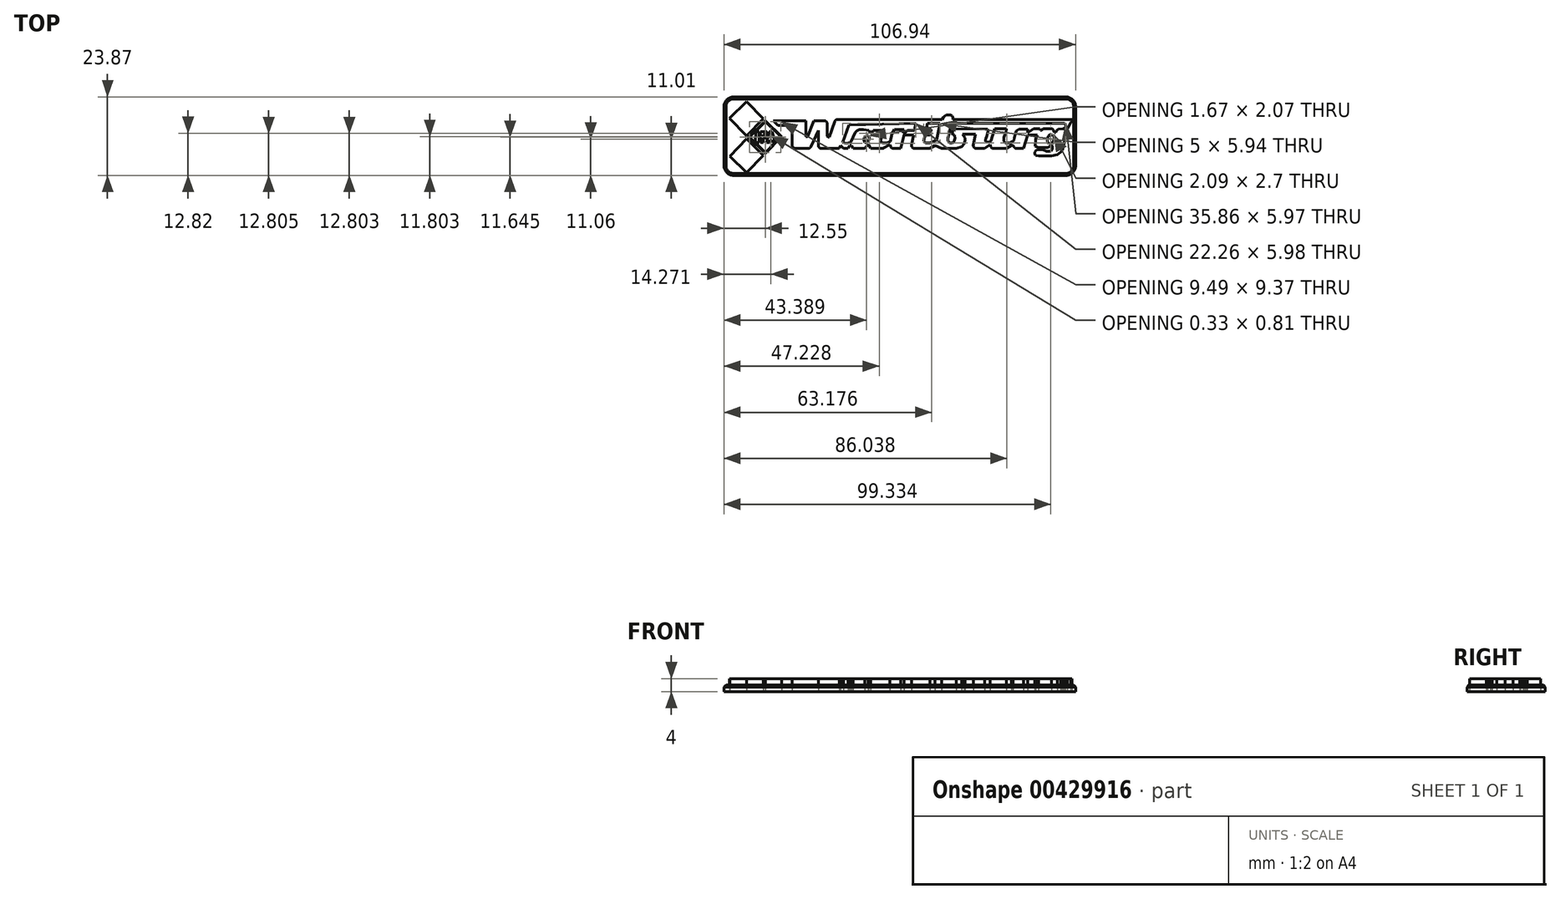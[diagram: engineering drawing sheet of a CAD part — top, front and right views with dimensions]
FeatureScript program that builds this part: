
annotation { "Feature Type Name" : "Feature", "Feature Type Description" : "" }
export const myFeature = defineFeature(function(context is Context, id is Id, definition is map)
    precondition{}
    {
        {
            var Q0;
            Q0=qCreatedBy(makeId("Top.planeOp"),FACE);
            var sketch = newSketch(context, id + "F0", { "sketchPlane" : qUnion([Q0])});
            skLineSegment(sketch, "E0", {"start": v(-43.55, 10.1) * mm, "end": v(-42.14, 8.69) * mm});
            skLineSegment(sketch, "E1", {"start": v(-42.14, 8.69) * mm, "end": v(-37.83, 8.69) * mm});
            skLineSegment(sketch, "E2", {"start": v(-37.83, 8.69) * mm, "end": v(-37.83, 2.66) * mm});
            skLineSegment(sketch, "E3", {"start": v(-36.83, 1.66) * mm, "end": v(-33.06, 1.66) * mm});
            skLineSegment(sketch, "E4", {"start": v(-32.15, 2.25) * mm, "end": v(-29.9, 7.18) * mm});
            skLineSegment(sketch, "E5", {"start": v(-29.9, 7.18) * mm, "end": v(-29.9, 2.66) * mm});
            skLineSegment(sketch, "E6", {"start": v(-28.9, 1.66) * mm, "end": v(-23.48, 1.66) * mm});
            skLineSegment(sketch, "E7", {"start": v(-23.48, 1.66) * mm, "end": v(-23.07, 2.58) * mm});
            skLineSegment(sketch, "E8", {"start": v(-23.07, 2.58) * mm, "end": v(-22.26, 1.66) * mm});
            skLineSegment(sketch, "E9", {"start": v(-22.26, 1.66) * mm, "end": v(-20.78, 1.66) * mm});
            skLineSegment(sketch, "E10", {"start": v(-20.78, 1.66) * mm, "end": v(-20.37, 2.58) * mm});
            skLineSegment(sketch, "E11", {"start": v(-20.37, 2.58) * mm, "end": v(-19.82, 2.58) * mm});
            skLineSegment(sketch, "E12", {"start": v(-19.82, 2.58) * mm, "end": v(-19.33, 1.66) * mm});
            skLineSegment(sketch, "E13", {"start": v(-19.33, 1.66) * mm, "end": v(-15.78, 1.66) * mm});
            skLineSegment(sketch, "E14", {"start": v(-15.78, 1.66) * mm, "end": v(-14.79, 2.94) * mm});
            skLineSegment(sketch, "E15", {"start": v(-14.79, 2.94) * mm, "end": v(-14.56, 2.83) * mm});
            skLineSegment(sketch, "E16", {"start": v(-14.56, 2.83) * mm, "end": v(-14.04, 1.66) * mm});
            skLineSegment(sketch, "E17", {"start": v(-14.04, 1.66) * mm, "end": v(-10.49, 1.66) * mm});
            skLineSegment(sketch, "E18", {"start": v(-10, 1.8) * mm, "end": v(-8.19, 2.83) * mm});
            skLineSegment(sketch, "E19", {"start": v(-8.19, 2.83) * mm, "end": v(-7.93, 2.26) * mm});
            skLineSegment(sketch, "E20", {"start": v(-7.02, 1.66) * mm, "end": v(-4.8, 1.66) * mm});
            skLineSegment(sketch, "E21", {"start": v(-4.8, 1.66) * mm, "end": v(-3.85, 5.72) * mm});
            skLineSegment(sketch, "E22", {"start": v(-3.85, 5.72) * mm, "end": v(-0.92, 5.72) * mm});
            skLineSegment(sketch, "E23", {"start": v(-0.92, 5.72) * mm, "end": v(-1.55, 2.88) * mm});
            skLineSegment(sketch, "E24", {"start": v(-0.57, 1.66) * mm, "end": v(4.03, 1.66) * mm});
            skLineSegment(sketch, "E25", {"start": v(4.03, 1.66) * mm, "end": v(5.61, 2.58) * mm});
            skLineSegment(sketch, "E26", {"start": v(5.61, 2.58) * mm, "end": v(7.62, 1.66) * mm});
            skLineSegment(sketch, "E27", {"start": v(7.62, 1.66) * mm, "end": v(12.02, 1.66) * mm});
            skLineSegment(sketch, "E28", {"start": v(12.02, 1.66) * mm, "end": v(13.67, 2.22) * mm});
            skLineSegment(sketch, "E29", {"start": v(13.67, 2.22) * mm, "end": v(14.43, 3.1) * mm});
            skLineSegment(sketch, "E30", {"start": v(14.43, 3.1) * mm, "end": v(14.66, 4.08) * mm});
            skLineSegment(sketch, "E31", {"start": v(14.66, 4.08) * mm, "end": v(14.66, 4.86) * mm});
            skLineSegment(sketch, "E32", {"start": v(14.66, 4.86) * mm, "end": v(14.32, 5.45) * mm});
            skLineSegment(sketch, "E33", {"start": v(14.32, 5.45) * mm, "end": v(13.97, 6.06) * mm});
            skLineSegment(sketch, "E34", {"start": v(13.97, 6.06) * mm, "end": v(17.89, 6.06) * mm});
            skLineSegment(sketch, "E35", {"start": v(17.89, 6.06) * mm, "end": v(17.22, 2.87) * mm});
            skLineSegment(sketch, "E36", {"start": v(18.2, 1.66) * mm, "end": v(20.67, 1.66) * mm});
            skLineSegment(sketch, "E37", {"start": v(20.67, 1.66) * mm, "end": v(22.38, 2.83) * mm});
            skLineSegment(sketch, "E38", {"start": v(22.38, 2.83) * mm, "end": v(22.43, 2.52) * mm});
            skLineSegment(sketch, "E39", {"start": v(23.42, 1.66) * mm, "end": v(27.3, 1.66) * mm});
            skLineSegment(sketch, "E40", {"start": v(27.3, 1.66) * mm, "end": v(28.86, 2.56) * mm});
            skLineSegment(sketch, "E41", {"start": v(28.86, 2.56) * mm, "end": v(29.36, 2.56) * mm});
            skLineSegment(sketch, "E42", {"start": v(29.36, 2.56) * mm, "end": v(29.59, 2.17) * mm});
            skLineSegment(sketch, "E43", {"start": v(30.45, 1.66) * mm, "end": v(32.55, 1.66) * mm});
            skLineSegment(sketch, "E44", {"start": v(32.55, 1.66) * mm, "end": v(33.8, 5.8) * mm});
            skLineSegment(sketch, "E45", {"start": v(33.8, 5.8) * mm, "end": v(36.68, 5.8) * mm});
            skLineSegment(sketch, "E46", {"start": v(36.68, 5.8) * mm, "end": v(36.24, 4.52) * mm});
            skLineSegment(sketch, "E47", {"start": v(36.24, 4.52) * mm, "end": v(36.05, 2.39) * mm});
            skLineSegment(sketch, "E48", {"start": v(36.05, 2.39) * mm, "end": v(37.02, 1.95) * mm});
            skLineSegment(sketch, "E49", {"start": v(37.02, 1.95) * mm, "end": v(40.01, 1.95) * mm});
            skLineSegment(sketch, "E50", {"start": v(40.01, 1.95) * mm, "end": v(40.77, 2.56) * mm});
            skLineSegment(sketch, "E51", {"start": v(40.77, 2.56) * mm, "end": v(41.17, 2.56) * mm});
            skLineSegment(sketch, "E52", {"start": v(41.17, 2.56) * mm, "end": v(41.33, 2.49) * mm});
            skLineSegment(sketch, "E53", {"start": v(41.33, 2.49) * mm, "end": v(41.33, 1.66) * mm});
            skLineSegment(sketch, "E54", {"start": v(41.33, 1.66) * mm, "end": v(40.92, 0.77) * mm});
            skLineSegment(sketch, "E55", {"start": v(40.92, 0.77) * mm, "end": v(39.5, 0.77) * mm});
            skLineSegment(sketch, "E56", {"start": v(39.5, 0.77) * mm, "end": v(38.83, 1.08) * mm});
            skLineSegment(sketch, "E57", {"start": v(38.83, 1.08) * mm, "end": v(38.33, 1.31) * mm});
            skLineSegment(sketch, "E58", {"start": v(38.33, 1.31) * mm, "end": v(36.74, 1.31) * mm});
            skLineSegment(sketch, "E59", {"start": v(36.74, 1.31) * mm, "end": v(36.28, 1.04) * mm});
            skLineSegment(sketch, "E60", {"start": v(36.28, 1.04) * mm, "end": v(35.88, 0.62) * mm});
            skLineSegment(sketch, "E61", {"start": v(35.88, 0.62) * mm, "end": v(35.88, 0) * mm});
            skLineSegment(sketch, "E62", {"start": v(35.88, 0) * mm, "end": v(36.14, -0.46) * mm});
            skLineSegment(sketch, "E63", {"start": v(36.14, -0.46) * mm, "end": v(37.02, -0.63) * mm});
            skLineSegment(sketch, "E64", {"start": v(37.02, -0.63) * mm, "end": v(39.02, -0.63) * mm});
            skLineSegment(sketch, "E65", {"start": v(39.02, -0.63) * mm, "end": v(41, -0.63) * mm});
            skLineSegment(sketch, "E66", {"start": v(41, -0.63) * mm, "end": v(42.73, -0.23) * mm});
            skLineSegment(sketch, "E67", {"start": v(42.73, -0.23) * mm, "end": v(43.85, 0.62) * mm});
            skLineSegment(sketch, "E68", {"start": v(43.85, 0.62) * mm, "end": v(44.3, 1.19) * mm});
            skLineSegment(sketch, "E69", {"start": v(44.3, 1.19) * mm, "end": v(44.65, 2.56) * mm});
            skLineSegment(sketch, "E70", {"start": v(44.65, 2.56) * mm, "end": v(45.18, 5.05) * mm});
            skLineSegment(sketch, "E71", {"start": v(45.18, 5.05) * mm, "end": v(45.85, 7.5) * mm});
            skLineSegment(sketch, "E72", {"start": v(45.85, 7.5) * mm, "end": v(46.42, 8.72) * mm});
            skLineSegment(sketch, "E73", {"start": v(46.42, 8.72) * mm, "end": v(46.81, 9.59) * mm});
            skLineSegment(sketch, "E74", {"start": v(46.81, 9.59) * mm, "end": v(47.17, 9.8) * mm});
            skLineSegment(sketch, "E75", {"start": v(47.17, 9.8) * mm, "end": v(47.17, 10.53) * mm});
            skLineSegment(sketch, "E76", {"start": v(47.17, 10.53) * mm, "end": v(11.1, 10.53) * mm});
            skLineSegment(sketch, "E77", {"start": v(11.1, 10.53) * mm, "end": v(11.1, 11.1) * mm});
            skLineSegment(sketch, "E78", {"start": v(11.1, 11.1) * mm, "end": v(10.83, 11.57) * mm});
            skLineSegment(sketch, "E79", {"start": v(10.83, 11.57) * mm, "end": v(10.27, 11.83) * mm});
            skLineSegment(sketch, "E80", {"start": v(10.27, 11.83) * mm, "end": v(9.03, 11.83) * mm});
            skLineSegment(sketch, "E81", {"start": v(9.03, 11.83) * mm, "end": v(8.48, 11.51) * mm});
            skLineSegment(sketch, "E82", {"start": v(8.48, 11.51) * mm, "end": v(8.06, 11.08) * mm});
            skLineSegment(sketch, "E83", {"start": v(8.06, 11.08) * mm, "end": v(7.67, 10.53) * mm});
            skLineSegment(sketch, "E84", {"start": v(7.67, 10.53) * mm, "end": v(-24, 10.53) * mm});
            skLineSegment(sketch, "E85", {"start": v(-24.94, 9.85) * mm, "end": v(-26.57, 5.09) * mm});
            skLineSegment(sketch, "E86", {"start": v(-26.57, 5.09) * mm, "end": v(-26.99, 5.09) * mm});
            skLineSegment(sketch, "E87", {"start": v(-26.99, 5.09) * mm, "end": v(-27.15, 5.37) * mm});
            skLineSegment(sketch, "E88", {"start": v(-27.15, 5.37) * mm, "end": v(-27.15, 9.1) * mm});
            skLineSegment(sketch, "E89", {"start": v(-28.15, 10.1) * mm, "end": v(-31.3, 10.1) * mm});
            skLineSegment(sketch, "E90", {"start": v(-31.3, 10.1) * mm, "end": v(-33.2, 5.32) * mm});
            skLineSegment(sketch, "E91", {"start": v(-33.2, 5.32) * mm, "end": v(-33.63, 5.32) * mm});
            skLineSegment(sketch, "E92", {"start": v(-33.63, 5.32) * mm, "end": v(-33.63, 10.1) * mm});
            skLineSegment(sketch, "E93", {"start": v(-33.63, 10.1) * mm, "end": v(-43.55, 10.1) * mm});
            skLineSegment(sketch, "E94", {"start": v(-45.97, 10.1) * mm, "end": v(-41.01, 5.28) * mm});
            skLineSegment(sketch, "E95", {"start": v(-41.01, 5.28) * mm, "end": v(-45.99, 0.15) * mm});
            skLineSegment(sketch, "E96", {"start": v(-48.96, 6.84) * mm, "end": v(-47.95, 6.84) * mm});
            skLineSegment(sketch, "E97", {"start": v(-47.95, 6.84) * mm, "end": v(-47.95, 3.5) * mm});
            skLineSegment(sketch, "E98", {"start": v(-47.95, 3.5) * mm, "end": v(-49, 3.5) * mm});
            skLineSegment(sketch, "E99", {"start": v(-49, 3.5) * mm, "end": v(-48.96, 6.84) * mm});
            skLineSegment(sketch, "E100", {"start": v(-47.5, 6.84) * mm, "end": v(-47.5, 3.5) * mm});
            skLineSegment(sketch, "E101", {"start": v(-47.5, 3.5) * mm, "end": v(-46.64, 3.5) * mm});
            skLineSegment(sketch, "E102", {"start": v(-46.64, 3.5) * mm, "end": v(-46.65, 4.88) * mm});
            skLineSegment(sketch, "E103", {"start": v(-46.65, 4.88) * mm, "end": v(-45.72, 4.88) * mm});
            skLineSegment(sketch, "E104", {"start": v(-45.72, 4.88) * mm, "end": v(-45.72, 5.57) * mm});
            skLineSegment(sketch, "E105", {"start": v(-45.72, 5.57) * mm, "end": v(-46.65, 5.57) * mm});
            skLineSegment(sketch, "E106", {"start": v(-46.65, 5.57) * mm, "end": v(-46.65, 5.85) * mm});
            skLineSegment(sketch, "E107", {"start": v(-46.65, 5.85) * mm, "end": v(-45.46, 5.85) * mm});
            skLineSegment(sketch, "E108", {"start": v(-45.46, 5.85) * mm, "end": v(-45.46, 6.84) * mm});
            skLineSegment(sketch, "E109", {"start": v(-45.46, 6.84) * mm, "end": v(-47.5, 6.84) * mm});
            skLineSegment(sketch, "E110", {"start": v(-44.77, 3.5) * mm, "end": v(-44.6, 4.3) * mm});
            skLineSegment(sketch, "E111", {"start": v(-44.6, 4.3) * mm, "end": v(-44.08, 4.3) * mm});
            skLineSegment(sketch, "E112", {"start": v(-44.08, 4.3) * mm, "end": v(-43.79, 3.5) * mm});
            skLineSegment(sketch, "E113", {"start": v(-43.79, 3.5) * mm, "end": v(-43.01, 3.5) * mm});
            skLineSegment(sketch, "E114", {"start": v(-43, 3.53) * mm, "end": v(-44.02, 6.84) * mm});
            skLineSegment(sketch, "E115", {"start": v(-44.02, 6.84) * mm, "end": v(-44.82, 6.84) * mm});
            skLineSegment(sketch, "E116", {"start": v(-44.82, 6.84) * mm, "end": v(-45.64, 3.5) * mm});
            skLineSegment(sketch, "E117", {"start": v(-45.64, 3.5) * mm, "end": v(-44.77, 3.5) * mm});
            skLineSegment(sketch, "E118", {"start": v(-44.48, 4.88) * mm, "end": v(-44.3, 5.69) * mm});
            skLineSegment(sketch, "E119", {"start": v(-44.3, 5.69) * mm, "end": v(-44.16, 4.88) * mm});
            skLineSegment(sketch, "E120", {"start": v(-44.16, 4.88) * mm, "end": v(-44.48, 4.88) * mm});
            skLineSegment(sketch, "E121", {"start": v(-51.66, 5.57) * mm, "end": v(-56.85, 10.86) * mm});
            skLineSegment(sketch, "E122", {"start": v(-56.85, 10.86) * mm, "end": v(-51.72, 15.9) * mm});
            skLineSegment(sketch, "E123", {"start": v(-51.72, 15.9) * mm, "end": v(-46.65, 10.73) * mm});
            skLineSegment(sketch, "E124", {"start": v(-46.65, 10.73) * mm, "end": v(-51.66, 5.57) * mm});
            skLineSegment(sketch, "E125", {"start": v(-51.66, 4.6) * mm, "end": v(-56.78, -0.67) * mm});
            skLineSegment(sketch, "E126", {"start": v(-56.78, -0.67) * mm, "end": v(-51.66, -5.64) * mm});
            skLineSegment(sketch, "E127", {"start": v(-51.66, -5.64) * mm, "end": v(-46.65, -0.48) * mm});
            skLineSegment(sketch, "E128", {"start": v(-46.65, -0.48) * mm, "end": v(-51.66, 4.6) * mm});
            skLineSegment(sketch, "E129", {"start": v(-22.5, 3.5) * mm, "end": v(-20.59, 8.84) * mm});
            skLineSegment(sketch, "E130", {"start": v(-20.59, 8.84) * mm, "end": v(-0.23, 9.27) * mm});
            skLineSegment(sketch, "E131", {"start": v(-0.23, 9.27) * mm, "end": v(-0.67, 7.2) * mm});
            skLineSegment(sketch, "E132", {"start": v(-0.67, 7.2) * mm, "end": v(-2.77, 7.2) * mm});
            skLineSegment(sketch, "E133", {"start": v(-2.77, 7.2) * mm, "end": v(-3.71, 6.28) * mm});
            skLineSegment(sketch, "E134", {"start": v(-3.71, 6.28) * mm, "end": v(-4.06, 6.28) * mm});
            skLineSegment(sketch, "E135", {"start": v(-4.06, 6.28) * mm, "end": v(-3.83, 7.38) * mm});
            skLineSegment(sketch, "E136", {"start": v(-3.83, 7.38) * mm, "end": v(-6.72, 7.38) * mm});
            skLineSegment(sketch, "E137", {"start": v(-6.72, 7.38) * mm, "end": v(-7.56, 6.13) * mm});
            skLineSegment(sketch, "E138", {"start": v(-7.56, 6.13) * mm, "end": v(-7.88, 4.6) * mm});
            skLineSegment(sketch, "E139", {"start": v(-7.88, 4.6) * mm, "end": v(-8.07, 3.71) * mm});
            skLineSegment(sketch, "E140", {"start": v(-8.07, 3.71) * mm, "end": v(-9.11, 3.32) * mm});
            skLineSegment(sketch, "E141", {"start": v(-9.11, 3.32) * mm, "end": v(-10.25, 3.32) * mm});
            skLineSegment(sketch, "E142", {"start": v(-10.25, 3.32) * mm, "end": v(-10.66, 3.5) * mm});
            skLineSegment(sketch, "E143", {"start": v(-10.66, 3.5) * mm, "end": v(-10.88, 4.12) * mm});
            skLineSegment(sketch, "E144", {"start": v(-10.88, 4.12) * mm, "end": v(-10.68, 5.09) * mm});
            skLineSegment(sketch, "E145", {"start": v(-10.68, 5.09) * mm, "end": v(-10.23, 6.06) * mm});
            skLineSegment(sketch, "E146", {"start": v(-10.23, 6.06) * mm, "end": v(-10.24, 7.13) * mm});
            skLineSegment(sketch, "E147", {"start": v(-10.24, 7.13) * mm, "end": v(-13.27, 7.13) * mm});
            skLineSegment(sketch, "E148", {"start": v(-13.27, 7.13) * mm, "end": v(-13.67, 6.25) * mm});
            skLineSegment(sketch, "E149", {"start": v(-13.67, 6.25) * mm, "end": v(-13.98, 6.25) * mm});
            skLineSegment(sketch, "E150", {"start": v(-13.98, 6.25) * mm, "end": v(-14.48, 7.13) * mm});
            skLineSegment(sketch, "E151", {"start": v(-14.48, 7.13) * mm, "end": v(-16.16, 7.38) * mm});
            skLineSegment(sketch, "E152", {"start": v(-16.16, 7.38) * mm, "end": v(-17.4, 7.38) * mm});
            skLineSegment(sketch, "E153", {"start": v(-17.4, 7.38) * mm, "end": v(-18.22, 7.08) * mm});
            skLineSegment(sketch, "E154", {"start": v(-18.22, 7.08) * mm, "end": v(-18.7, 6.6) * mm});
            skLineSegment(sketch, "E155", {"start": v(-18.7, 6.6) * mm, "end": v(-19.07, 5.76) * mm});
            skLineSegment(sketch, "E156", {"start": v(-19.07, 5.76) * mm, "end": v(-19.47, 4.88) * mm});
            skLineSegment(sketch, "E157", {"start": v(-19.47, 4.88) * mm, "end": v(-19.99, 3.75) * mm});
            skLineSegment(sketch, "E158", {"start": v(-19.99, 3.75) * mm, "end": v(-20.23, 3.5) * mm});
            skLineSegment(sketch, "E159", {"start": v(-20.23, 3.5) * mm, "end": v(-21.34, 3.3) * mm});
            skLineSegment(sketch, "E160", {"start": v(-21.34, 3.3) * mm, "end": v(-22.5, 3.5) * mm});
            skLineSegment(sketch, "E161", {"start": v(-14.76, 5.57) * mm, "end": v(-15.36, 5.57) * mm});
            skLineSegment(sketch, "E162", {"start": v(-15.36, 5.57) * mm, "end": v(-16.04, 4.88) * mm});
            skLineSegment(sketch, "E163", {"start": v(-16.04, 4.88) * mm, "end": v(-16.03, 4.3) * mm});
            skLineSegment(sketch, "E164", {"start": v(-16.03, 4.3) * mm, "end": v(-15.74, 3.5) * mm});
            skLineSegment(sketch, "E165", {"start": v(-15.74, 3.5) * mm, "end": v(-15.52, 3.5) * mm});
            skLineSegment(sketch, "E166", {"start": v(-15.52, 3.5) * mm, "end": v(-14.73, 3.8) * mm});
            skLineSegment(sketch, "E167", {"start": v(-14.73, 3.8) * mm, "end": v(-14.37, 4.6) * mm});
            skLineSegment(sketch, "E168", {"start": v(-14.37, 4.6) * mm, "end": v(-14.37, 5.09) * mm});
            skLineSegment(sketch, "E169", {"start": v(-14.37, 5.09) * mm, "end": v(-14.76, 5.57) * mm});
            skLineSegment(sketch, "E170", {"start": v(3.25, 9.27) * mm, "end": v(2.85, 7.38) * mm});
            skLineSegment(sketch, "E171", {"start": v(2.85, 7.38) * mm, "end": v(4.38, 7.38) * mm});
            skLineSegment(sketch, "E172", {"start": v(4.38, 7.38) * mm, "end": v(4, 5.72) * mm});
            skLineSegment(sketch, "E173", {"start": v(4, 5.72) * mm, "end": v(2.47, 5.72) * mm});
            skLineSegment(sketch, "E174", {"start": v(2.47, 5.72) * mm, "end": v(2.09, 3.9) * mm});
            skLineSegment(sketch, "E175", {"start": v(2.09, 3.9) * mm, "end": v(2.68, 3.33) * mm});
            skLineSegment(sketch, "E176", {"start": v(2.68, 3.33) * mm, "end": v(3.87, 3.33) * mm});
            skLineSegment(sketch, "E177", {"start": v(3.87, 3.33) * mm, "end": v(5.19, 3.82) * mm});
            skLineSegment(sketch, "E178", {"start": v(5.19, 3.82) * mm, "end": v(6.03, 4.3) * mm});
            skLineSegment(sketch, "E179", {"start": v(6.03, 4.3) * mm, "end": v(7.09, 9.27) * mm});
            skLineSegment(sketch, "E180", {"start": v(7.09, 9.27) * mm, "end": v(3.25, 9.27) * mm});
            skLineSegment(sketch, "E181", {"start": v(10.81, 9.27) * mm, "end": v(44.92, 9.27) * mm});
            skLineSegment(sketch, "E182", {"start": v(44.92, 9.27) * mm, "end": v(45.38, 8.83) * mm});
            skLineSegment(sketch, "E183", {"start": v(45.38, 8.83) * mm, "end": v(45.38, 8.3) * mm});
            skLineSegment(sketch, "E184", {"start": v(45.38, 8.3) * mm, "end": v(45.32, 8.03) * mm});
            skLineSegment(sketch, "E185", {"start": v(45.32, 8.03) * mm, "end": v(44.62, 7.63) * mm});
            skLineSegment(sketch, "E186", {"start": v(44.62, 7.63) * mm, "end": v(43.1, 7.5) * mm});
            skLineSegment(sketch, "E187", {"start": v(43.1, 7.5) * mm, "end": v(42.55, 6.98) * mm});
            skLineSegment(sketch, "E188", {"start": v(42.55, 6.98) * mm, "end": v(42.34, 6.49) * mm});
            skLineSegment(sketch, "E189", {"start": v(42.34, 6.49) * mm, "end": v(41.9, 6.49) * mm});
            skLineSegment(sketch, "E190", {"start": v(41.9, 6.49) * mm, "end": v(41.7, 7.16) * mm});
            skLineSegment(sketch, "E191", {"start": v(41.7, 7.16) * mm, "end": v(41.26, 7.63) * mm});
            skLineSegment(sketch, "E192", {"start": v(41.26, 7.63) * mm, "end": v(38.42, 7.63) * mm});
            skLineSegment(sketch, "E193", {"start": v(38.42, 7.63) * mm, "end": v(37.95, 7.13) * mm});
            skLineSegment(sketch, "E194", {"start": v(37.95, 7.13) * mm, "end": v(37.75, 7.13) * mm});
            skLineSegment(sketch, "E195", {"start": v(37.75, 7.13) * mm, "end": v(37.48, 7.63) * mm});
            skLineSegment(sketch, "E196", {"start": v(37.48, 7.63) * mm, "end": v(35.55, 7.63) * mm});
            skLineSegment(sketch, "E197", {"start": v(35.55, 7.63) * mm, "end": v(33.96, 6.49) * mm});
            skLineSegment(sketch, "E198", {"start": v(33.96, 6.49) * mm, "end": v(33.75, 6.49) * mm});
            skLineSegment(sketch, "E199", {"start": v(33.75, 6.49) * mm, "end": v(33.75, 7.52) * mm});
            skLineSegment(sketch, "E200", {"start": v(33.75, 7.52) * mm, "end": v(31.06, 7.52) * mm});
            skLineSegment(sketch, "E201", {"start": v(31.06, 7.52) * mm, "end": v(30.32, 7.1) * mm});
            skLineSegment(sketch, "E202", {"start": v(30.32, 7.1) * mm, "end": v(29.93, 5.86) * mm});
            skLineSegment(sketch, "E203", {"start": v(29.93, 5.86) * mm, "end": v(29.77, 4.9) * mm});
            skLineSegment(sketch, "E204", {"start": v(29.77, 4.9) * mm, "end": v(29.57, 4.15) * mm});
            skLineSegment(sketch, "E205", {"start": v(29.57, 4.15) * mm, "end": v(29, 3.7) * mm});
            skLineSegment(sketch, "E206", {"start": v(29, 3.7) * mm, "end": v(28.41, 3.42) * mm});
            skLineSegment(sketch, "E207", {"start": v(28.41, 3.42) * mm, "end": v(27.68, 3.42) * mm});
            skLineSegment(sketch, "E208", {"start": v(27.68, 3.42) * mm, "end": v(26.9, 3.42) * mm});
            skLineSegment(sketch, "E209", {"start": v(26.9, 3.42) * mm, "end": v(26.57, 3.84) * mm});
            skLineSegment(sketch, "E210", {"start": v(26.57, 3.84) * mm, "end": v(26.57, 5.06) * mm});
            skLineSegment(sketch, "E211", {"start": v(26.57, 5.06) * mm, "end": v(26.81, 5.77) * mm});
            skLineSegment(sketch, "E212", {"start": v(26.81, 5.77) * mm, "end": v(27.13, 6.43) * mm});
            skLineSegment(sketch, "E213", {"start": v(27.13, 6.43) * mm, "end": v(27.3, 7.63) * mm});
            skLineSegment(sketch, "E214", {"start": v(27.3, 7.63) * mm, "end": v(23.77, 7.63) * mm});
            skLineSegment(sketch, "E215", {"start": v(23.77, 7.63) * mm, "end": v(22.6, 3.94) * mm});
            skLineSegment(sketch, "E216", {"start": v(22.6, 3.94) * mm, "end": v(22.3, 3.7) * mm});
            skLineSegment(sketch, "E217", {"start": v(22.3, 3.7) * mm, "end": v(21.64, 3.57) * mm});
            skLineSegment(sketch, "E218", {"start": v(21.64, 3.57) * mm, "end": v(20.97, 3.7) * mm});
            skLineSegment(sketch, "E219", {"start": v(20.97, 3.7) * mm, "end": v(20.97, 4.2) * mm});
            skLineSegment(sketch, "E220", {"start": v(20.97, 4.2) * mm, "end": v(21.09, 4.8) * mm});
            skLineSegment(sketch, "E221", {"start": v(21.09, 4.8) * mm, "end": v(21.28, 5.44) * mm});
            skLineSegment(sketch, "E222", {"start": v(21.28, 5.44) * mm, "end": v(21.71, 6.92) * mm});
            skLineSegment(sketch, "E223", {"start": v(21.71, 6.92) * mm, "end": v(21.71, 7.26) * mm});
            skLineSegment(sketch, "E224", {"start": v(21.71, 7.26) * mm, "end": v(21.52, 7.51) * mm});
            skLineSegment(sketch, "E225", {"start": v(21.52, 7.51) * mm, "end": v(11.63, 7.63) * mm});
            skLineSegment(sketch, "E226", {"start": v(11.63, 7.63) * mm, "end": v(11.21, 7.3) * mm});
            skLineSegment(sketch, "E227", {"start": v(11.21, 7.3) * mm, "end": v(10.87, 6.79) * mm});
            skLineSegment(sketch, "E228", {"start": v(10.87, 6.79) * mm, "end": v(10.87, 6.14) * mm});
            skLineSegment(sketch, "E229", {"start": v(10.87, 6.14) * mm, "end": v(11.07, 5.73) * mm});
            skLineSegment(sketch, "E230", {"start": v(11.07, 5.73) * mm, "end": v(11.53, 5.73) * mm});
            skLineSegment(sketch, "E231", {"start": v(11.53, 5.73) * mm, "end": v(11.65, 4.8) * mm});
            skLineSegment(sketch, "E232", {"start": v(11.65, 4.8) * mm, "end": v(11.43, 4.01) * mm});
            skLineSegment(sketch, "E233", {"start": v(11.43, 4.01) * mm, "end": v(11.14, 3.54) * mm});
            skLineSegment(sketch, "E234", {"start": v(11.14, 3.54) * mm, "end": v(10.64, 3.3) * mm});
            skLineSegment(sketch, "E235", {"start": v(10.64, 3.3) * mm, "end": v(9.98, 3.3) * mm});
            skLineSegment(sketch, "E236", {"start": v(9.98, 3.3) * mm, "end": v(9.75, 3.58) * mm});
            skLineSegment(sketch, "E237", {"start": v(9.75, 3.58) * mm, "end": v(9.52, 4.08) * mm});
            skLineSegment(sketch, "E238", {"start": v(9.52, 4.08) * mm, "end": v(9.52, 4.85) * mm});
            skLineSegment(sketch, "E239", {"start": v(9.52, 4.85) * mm, "end": v(9.84, 6.19) * mm});
            skLineSegment(sketch, "E240", {"start": v(9.84, 6.19) * mm, "end": v(10.19, 7.37) * mm});
            skLineSegment(sketch, "E241", {"start": v(10.19, 7.37) * mm, "end": v(10.81, 9.27) * mm});
            skPoint(sketch, "E242.visualSharp", {"position": v(-37.83, 1.66) * mm});
            skArc(sketch, "E242.filletArc", {"start": v(-37.83, 2.66) * mm, "mid": v(-37.54, 1.96) * mm, "end": v(-36.83, 1.66) * mm});
            skPoint(sketch, "E243.visualSharp", {"position": v(-32.41, 1.66) * mm});
            skArc(sketch, "E243.filletArc", {"start": v(-33.06, 1.66) * mm, "mid": v(-32.51, 1.82) * mm, "end": v(-32.15, 2.25) * mm});
            skPoint(sketch, "E244.visualSharp", {"position": v(-29.9, 1.66) * mm});
            skArc(sketch, "E244.filletArc", {"start": v(-29.9, 2.66) * mm, "mid": v(-29.61, 1.96) * mm, "end": v(-28.9, 1.66) * mm});
            skPoint(sketch, "E245.visualSharp", {"position": v(-7.67, 1.66) * mm});
            skArc(sketch, "E245.filletArc", {"start": v(-7.93, 2.26) * mm, "mid": v(-7.56, 1.83) * mm, "end": v(-7.02, 1.66) * mm});
            skPoint(sketch, "E246.visualSharp", {"position": v(-10.22, 1.66) * mm});
            skArc(sketch, "E246.filletArc", {"start": v(-10.49, 1.66) * mm, "mid": v(-10.23, 1.7) * mm, "end": v(-10, 1.8) * mm});
            skPoint(sketch, "E247.visualSharp", {"position": v(-1.82, 1.66) * mm});
            skArc(sketch, "E247.filletArc", {"start": v(-1.55, 2.88) * mm, "mid": v(-1.35, 2.04) * mm, "end": v(-0.57, 1.66) * mm});
            skPoint(sketch, "E248.visualSharp", {"position": v(16.96, 1.66) * mm});
            skArc(sketch, "E248.filletArc", {"start": v(17.22, 2.87) * mm, "mid": v(17.42, 2.03) * mm, "end": v(18.2, 1.66) * mm});
            skPoint(sketch, "E249.visualSharp", {"position": v(22.55, 1.66) * mm});
            skArc(sketch, "E249.filletArc", {"start": v(22.43, 2.52) * mm, "mid": v(22.76, 1.9) * mm, "end": v(23.42, 1.66) * mm});
            skPoint(sketch, "E250.visualSharp", {"position": v(29.88, 1.66) * mm});
            skArc(sketch, "E250.filletArc", {"start": v(29.59, 2.17) * mm, "mid": v(29.95, 1.8) * mm, "end": v(30.45, 1.66) * mm});
            skLineSegment(sketch, "E251", {"start": v(40.8, 5.84) * mm, "end": v(40.17, 5.46) * mm});
            skLineSegment(sketch, "E252", {"start": v(40.17, 5.46) * mm, "end": v(39.7, 4.7) * mm});
            skLineSegment(sketch, "E253", {"start": v(39.7, 4.7) * mm, "end": v(39.7, 3.97) * mm});
            skLineSegment(sketch, "E254", {"start": v(39.7, 3.97) * mm, "end": v(39.9, 3.43) * mm});
            skLineSegment(sketch, "E255", {"start": v(39.9, 3.43) * mm, "end": v(40.33, 3.14) * mm});
            skLineSegment(sketch, "E256", {"start": v(40.33, 3.14) * mm, "end": v(41.08, 3.14) * mm});
            skLineSegment(sketch, "E257", {"start": v(41.08, 3.14) * mm, "end": v(41.63, 4.02) * mm});
            skLineSegment(sketch, "E258", {"start": v(41.63, 4.02) * mm, "end": v(41.79, 4.88) * mm});
            skLineSegment(sketch, "E259", {"start": v(41.79, 4.88) * mm, "end": v(41.79, 5.43) * mm});
            skLineSegment(sketch, "E260", {"start": v(41.79, 5.43) * mm, "end": v(41.5, 5.67) * mm});
            skLineSegment(sketch, "E261", {"start": v(41.5, 5.67) * mm, "end": v(40.8, 5.84) * mm});
            skLineSegment(sketch, "E262.0", {"start": v(-45.97, 9.81) * mm, "end": v(-41.3, 5.27) * mm});
            skLineSegment(sketch, "E263.0", {"start": v(-41.3, 5.27) * mm, "end": v(-43, 3.53) * mm});
            skLineSegment(sketch, "E264.0", {"start": v(-46, 0.44) * mm, "end": v(-50.78, 5.09) * mm});
            skLineSegment(sketch, "E265.trimOffspring", {"start": v(-50.78, 5.09) * mm, "end": v(-45.97, 9.81) * mm});
            skPoint(sketch, "E266.orphan", {"position": v(-51.07, 5.09) * mm});
            skLineSegment(sketch, "E267", {"start": v(-45.99, 0.15) * mm, "end": v(-51.07, 5.09) * mm});
            skLineSegment(sketch, "E268", {"start": v(-51.07, 5.09) * mm, "end": v(-45.97, 10.1) * mm});
            skLineSegment(sketch, "E269.trimOffspring", {"start": v(-43.01, 3.5) * mm, "end": v(-46, 0.44) * mm});
            skPoint(sketch, "E270.visualSharp", {"position": v(-24.7, 10.53) * mm});
            skArc(sketch, "E270.filletArc", {"start": v(-24, 10.53) * mm, "mid": v(-24.57, 10.34) * mm, "end": v(-24.94, 9.85) * mm});
            skPoint(sketch, "E271.visualSharp", {"position": v(-27.15, 10.1) * mm});
            skArc(sketch, "E271.filletArc", {"start": v(-27.15, 9.1) * mm, "mid": v(-27.44, 9.82) * mm, "end": v(-28.15, 10.1) * mm});
            skSolve(sketch);
        }
        {
            var Q0;
            Q0=makeQuery(id+"F0.imprint","IMPRINT",FACE,{"disambiguationData":[TD([[makeQuery(id+"F0.imprint","IMPRINT",EDGE,{"derivedFrom":sQuery(id+"F0.wireOp",EDGE,"E121")}),-1.0]])]});
            var Q1;
            Q1=makeQuery(id+"F0.imprint","IMPRINT",FACE,{"disambiguationData":[TD([[makeQuery(id+"F0.imprint","IMPRINT",EDGE,{"derivedFrom":sQuery(id+"F0.wireOp",EDGE,"E125")}),1.0]])]});
            var Q2;
            Q2=makeQuery(id+"F0.imprint","IMPRINT",FACE,{"disambiguationData":[TD([[makeQuery(id+"F0.imprint","IMPRINT",EDGE,{"derivedFrom":sQuery(id+"F0.wireOp",EDGE,"E94")}),-1.0]])]});
            var Q3;
            Q3=makeQuery(id+"F0.imprint","IMPRINT",FACE,{"disambiguationData":[TD([[makeQuery(id+"F0.imprint","IMPRINT",EDGE,{"derivedFrom":sQuery(id+"F0.wireOp",EDGE,"E100")}),1.0]])]});
            var Q4;
            Q4=makeQuery(id+"F0.imprint","IMPRINT",FACE,{"disambiguationData":[TD([[makeQuery(id+"F0.imprint","IMPRINT",EDGE,{"derivedFrom":sQuery(id+"F0.wireOp",EDGE,"E96")}),-1.0]])]});
            var Q5;
            Q5=makeQuery(id+"F0.imprint","IMPRINT",FACE,{"disambiguationData":[TD([[makeQuery(id+"F0.imprint","IMPRINT",EDGE,{"derivedFrom":sQuery(id+"F0.wireOp",EDGE,"E0")}),1.0]])]});
            extrude(context, id + "F1", {"entities" : qUnion([Q0, Q1, Q2, Q3, Q4, Q5]), "depth" : 4 * mm});
        }
        {
            var Q0;
            Q0=qCreatedBy(makeId("Top.planeOp"),FACE);
            var sketch = newSketch(context, id + "F2", { "sketchPlane" : qUnion([Q0])});
            skLineSegment(sketch, "E272.bottom", {"start": v(-55.59, 17.35) * mm, "end": v(45.35, 17.35) * mm});
            skLineSegment(sketch, "E272.top", {"start": v(-55.59, -6.52) * mm, "end": v(45.35, -6.52) * mm});
            skLineSegment(sketch, "E272.left", {"start": v(-58.59, 14.35) * mm, "end": v(-58.59, -3.52) * mm});
            skLineSegment(sketch, "E272.right", {"start": v(48.35, 14.35) * mm, "end": v(48.35, -3.52) * mm});
            skPoint(sketch, "E273.visualSharp", {"position": v(-58.59, 17.35) * mm});
            skArc(sketch, "E273.filletArc", {"start": v(-55.59, 17.35) * mm, "mid": v(-57.7, 16.47) * mm, "end": v(-58.59, 14.35) * mm});
            skPoint(sketch, "E274.visualSharp", {"position": v(48.35, 17.35) * mm});
            skArc(sketch, "E274.filletArc", {"start": v(48.35, 14.35) * mm, "mid": v(47.47, 16.47) * mm, "end": v(45.35, 17.35) * mm});
            skPoint(sketch, "E275.visualSharp", {"position": v(48.35, -6.52) * mm});
            skArc(sketch, "E275.filletArc", {"start": v(45.35, -6.52) * mm, "mid": v(47.47, -5.64) * mm, "end": v(48.35, -3.52) * mm});
            skPoint(sketch, "E276.visualSharp", {"position": v(-58.59, -6.52) * mm});
            skArc(sketch, "E276.filletArc", {"start": v(-58.59, -3.52) * mm, "mid": v(-57.7, -5.64) * mm, "end": v(-55.59, -6.52) * mm});
            skSolve(sketch);
        }
        {
            var Q0;
            Q0=makeQuery(id+"F2.imprint","IMPRINT",FACE,{"disambiguationData":[TD([[makeQuery(id+"F2.imprint","IMPRINT",EDGE,{"derivedFrom":sQuery(id+"F2.wireOp",EDGE,"E272.bottom")}),-1.0]])]});
            extrude(context, id + "F3", {"entities" : qUnion([Q0]), "depth" : 2 * mm});
        }
        {
            var Q0;
            Q0=makeQuery(id+"F3.opExtrude","CAP_EDGE",EDGE,{"disambiguationData":[OSD([sQuery(id+"F2.wireOp",EDGE,"E272.top")])],"isStart":false});
            var Q1;
            Q1=makeQuery(id+"F3.opExtrude","CAP_EDGE",EDGE,{"disambiguationData":[OSD([sQuery(id+"F2.wireOp",EDGE,"E276.filletArc")])],"isStart":false});
            var Q2;
            Q2=makeQuery(id+"F3.opExtrude","CAP_EDGE",EDGE,{"disambiguationData":[OSD([sQuery(id+"F2.wireOp",EDGE,"E272.left")])],"isStart":false});
            var Q3;
            Q3=makeQuery(id+"F3.opExtrude","CAP_EDGE",EDGE,{"disambiguationData":[OSD([sQuery(id+"F2.wireOp",EDGE,"E273.filletArc")])],"isStart":false});
            var Q4;
            Q4=makeQuery(id+"F3.opExtrude","CAP_EDGE",EDGE,{"disambiguationData":[OSD([sQuery(id+"F2.wireOp",EDGE,"E272.bottom")])],"isStart":false});
            var Q5;
            Q5=makeQuery(id+"F3.opExtrude","CAP_EDGE",EDGE,{"disambiguationData":[OSD([sQuery(id+"F2.wireOp",EDGE,"E274.filletArc")])],"isStart":false});
            var Q6;
            Q6=makeQuery(id+"F3.opExtrude","CAP_EDGE",EDGE,{"disambiguationData":[OSD([sQuery(id+"F2.wireOp",EDGE,"E272.right")])],"isStart":false});
            var Q7;
            Q7=makeQuery(id+"F3.opExtrude","CAP_EDGE",EDGE,{"disambiguationData":[OSD([sQuery(id+"F2.wireOp",EDGE,"E275.filletArc")])],"isStart":false});
            chamfer(context, id + "F4", {"entities" : qUnion([Q0, Q1, Q2, Q3, Q4, Q5, Q6, Q7]), "width" : 0.6 * mm, "tangentPropagation" : true});
        }
    });
